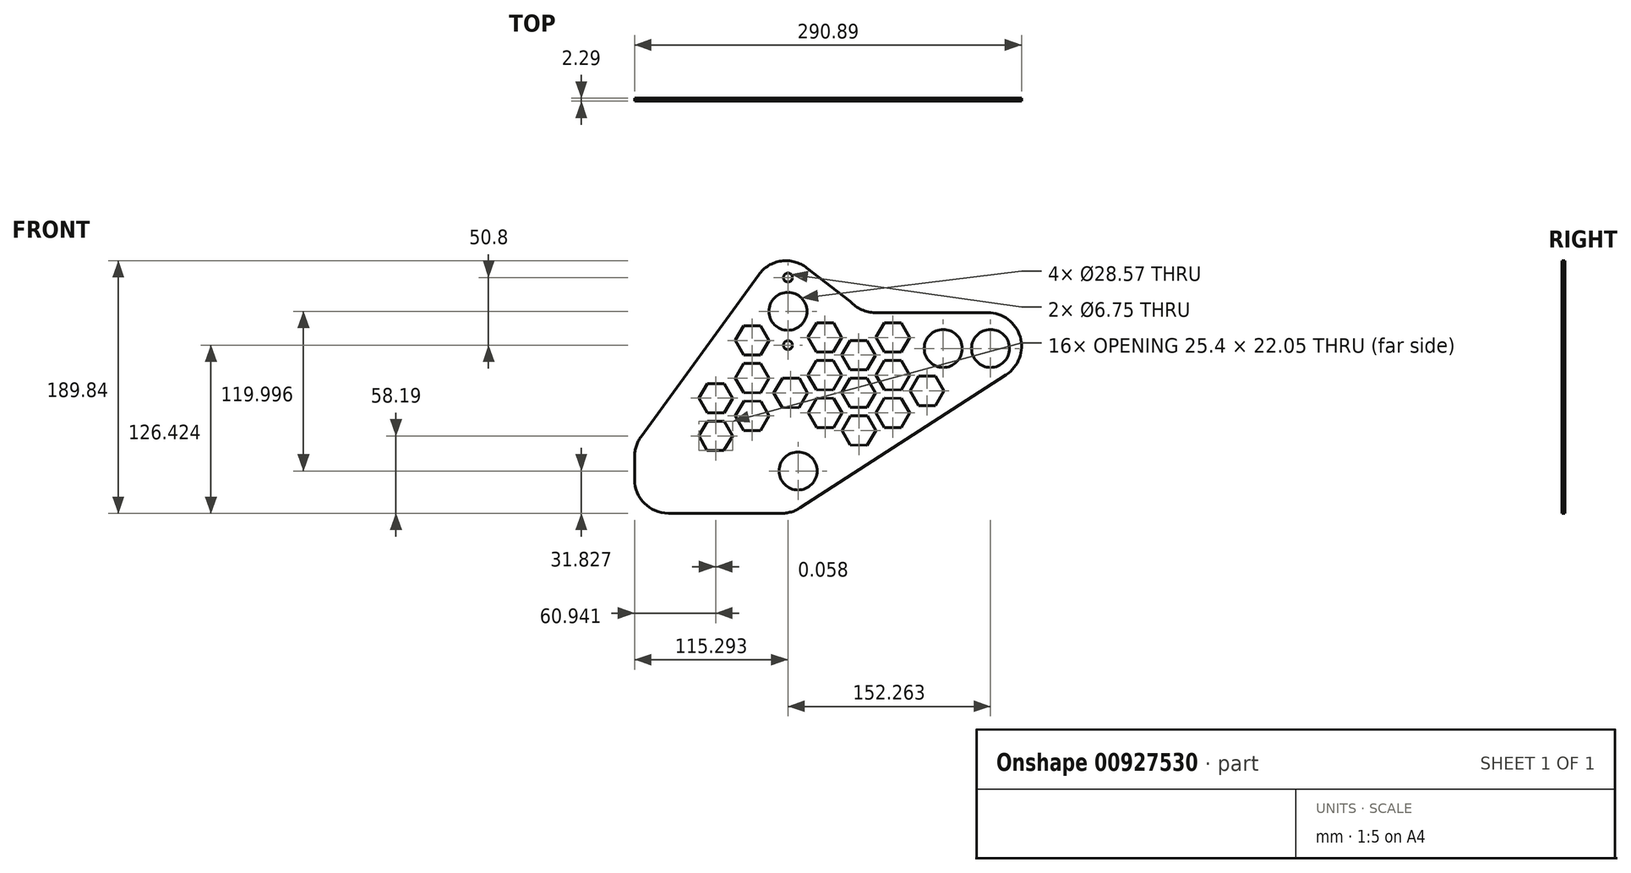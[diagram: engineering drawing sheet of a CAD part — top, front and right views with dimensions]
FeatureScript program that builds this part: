
annotation { "Feature Type Name" : "Feature", "Feature Type Description" : "" }
export const myFeature = defineFeature(function(context is Context, id is Id, definition is map)
    precondition{}
    {
        {
            var Q0;
            Q0=qCreatedBy(makeId("Front.planeOp"),FACE);
            var sketch = newSketch(context, id + "F0", { "sketchPlane" : qUnion([Q0])});
            skCircle(sketch, "E0", {"center": v(124.42, 56.16) * mm, "radius": 14.29 * mm});
            skCircle(sketch, "E1", {"center": v(88.86, 56.16) * mm, "radius": 14.29 * mm});
            skCircle(sketch, "E2", {"center": v(-27.85, 84.08) * mm, "radius": 14.29 * mm});
            skCircle(sketch, "E3", {"center": v(-20.21, -35.91) * mm, "radius": 14.29 * mm});
            skLineSegment(sketch, "E4", {"start": v(189.17, -93.06) * mm, "end": v(-151.78, -93.06) * mm});
            skCircle(sketch, "E5", {"center": v(-27.85, 109.48) * mm, "radius": 3.37 * mm});
            skCircle(sketch, "E6", {"center": v(-27.85, 58.68) * mm, "radius": 3.37 * mm});
            skLineSegment(sketch, "E7", {"start": v(-18.82, -63.68) * mm, "end": v(136.13, 36.41) * mm});
            skLineSegment(sketch, "E8", {"start": v(37.84, 83.15) * mm, "end": v(122.35, 83.15) * mm});
            skPoint(sketch, "E9.visualSharp", {"position": v(208.48, 83.15) * mm});
            skArc(sketch, "E9.filletArc", {"start": v(136.13, 36.41) * mm, "mid": v(146.71, 64.93) * mm, "end": v(122.35, 83.15) * mm});
            skPoint(sketch, "E10.visualSharp", {"position": v(26.59, 83.15) * mm});
            skArc(sketch, "E10.filletArc", {"start": v(19.03, 91.48) * mm, "mid": v(27.55, 85.33) * mm, "end": v(37.84, 83.15) * mm});
            skPoint(sketch, "E11.visualSharp", {"position": v(-170.89, -139.65) * mm});
            skPoint(sketch, "E12.visualSharp", {"position": v(-106.56, -106.37) * mm});
            skPoint(sketch, "E13.visualSharp", {"position": v(-22.67, -66.16) * mm});
            skArc(sketch, "E13.filletArc", {"start": v(-34.57, -67.66) * mm, "mid": v(-26.37, -66.96) * mm, "end": v(-18.82, -63.68) * mm});
            skCircle(sketch, "E14.cCircle", {"center": v(50.95, 64.44) * mm, "radius": 11 * mm, "construction": true});
            skLineSegment(sketch, "E14.0", {"start": v(44.55, 53.47) * mm, "end": v(38.25, 64.5) * mm});
            skLineSegment(sketch, "E14.1", {"start": v(38.25, 64.5) * mm, "end": v(44.64, 75.47) * mm});
            skLineSegment(sketch, "E14.2", {"start": v(44.64, 75.47) * mm, "end": v(57.34, 75.41) * mm});
            skLineSegment(sketch, "E14.3", {"start": v(57.34, 75.41) * mm, "end": v(63.65, 64.39) * mm});
            skLineSegment(sketch, "E14.4", {"start": v(63.65, 64.39) * mm, "end": v(57.25, 53.42) * mm});
            skLineSegment(sketch, "E14.5", {"start": v(57.25, 53.42) * mm, "end": v(44.55, 53.47) * mm});
            skPoint(sketch, "E14.0.midPoint", {"position": v(41.4, 58.99) * mm});
            skCircle(sketch, "E15.cCircle", {"center": v(50.89, 36.1) * mm, "radius": 11 * mm, "construction": true});
            skLineSegment(sketch, "E15.0", {"start": v(44.49, 25.13) * mm, "end": v(38.19, 36.15) * mm});
            skLineSegment(sketch, "E15.1", {"start": v(38.19, 36.15) * mm, "end": v(44.59, 47.12) * mm});
            skLineSegment(sketch, "E15.2", {"start": v(44.59, 47.12) * mm, "end": v(57.29, 47.07) * mm});
            skLineSegment(sketch, "E15.3", {"start": v(57.29, 47.07) * mm, "end": v(63.59, 36.04) * mm});
            skLineSegment(sketch, "E15.4", {"start": v(63.59, 36.04) * mm, "end": v(57.19, 25.07) * mm});
            skLineSegment(sketch, "E15.5", {"start": v(57.19, 25.07) * mm, "end": v(44.49, 25.13) * mm});
            skPoint(sketch, "E15.0.midPoint", {"position": v(41.34, 30.64) * mm});
            skCircle(sketch, "E16.cCircle", {"center": v(51.04, 7.75) * mm, "radius": 11 * mm, "construction": true});
            skLineSegment(sketch, "E16.0", {"start": v(44.64, -3.22) * mm, "end": v(38.34, 7.8) * mm});
            skLineSegment(sketch, "E16.1", {"start": v(38.34, 7.8) * mm, "end": v(44.74, 18.78) * mm});
            skLineSegment(sketch, "E16.2", {"start": v(44.74, 18.78) * mm, "end": v(57.44, 18.72) * mm});
            skLineSegment(sketch, "E16.3", {"start": v(57.44, 18.72) * mm, "end": v(63.74, 7.7) * mm});
            skLineSegment(sketch, "E16.4", {"start": v(63.74, 7.7) * mm, "end": v(57.34, -3.28) * mm});
            skLineSegment(sketch, "E16.5", {"start": v(57.34, -3.28) * mm, "end": v(44.64, -3.22) * mm});
            skPoint(sketch, "E16.0.midPoint", {"position": v(41.5, 2.3) * mm});
            skCircle(sketch, "E17.cCircle", {"center": v(25.33, 51.18) * mm, "radius": 11 * mm, "construction": true});
            skLineSegment(sketch, "E17.0", {"start": v(18.93, 40.2) * mm, "end": v(12.63, 51.23) * mm});
            skLineSegment(sketch, "E17.1", {"start": v(12.63, 51.23) * mm, "end": v(19.03, 62.2) * mm});
            skLineSegment(sketch, "E17.2", {"start": v(19.03, 62.2) * mm, "end": v(31.73, 62.15) * mm});
            skLineSegment(sketch, "E17.3", {"start": v(31.73, 62.15) * mm, "end": v(38.03, 51.12) * mm});
            skLineSegment(sketch, "E17.4", {"start": v(38.03, 51.12) * mm, "end": v(31.63, 40.15) * mm});
            skLineSegment(sketch, "E17.5", {"start": v(31.63, 40.15) * mm, "end": v(18.93, 40.2) * mm});
            skPoint(sketch, "E17.0.midPoint", {"position": v(15.78, 45.72) * mm});
            skCircle(sketch, "E18.cCircle", {"center": v(25.27, 22.83) * mm, "radius": 11 * mm, "construction": true});
            skLineSegment(sketch, "E18.0", {"start": v(18.87, 11.86) * mm, "end": v(12.57, 22.89) * mm});
            skLineSegment(sketch, "E18.1", {"start": v(12.57, 22.89) * mm, "end": v(18.97, 33.86) * mm});
            skLineSegment(sketch, "E18.2", {"start": v(18.97, 33.86) * mm, "end": v(31.67, 33.8) * mm});
            skLineSegment(sketch, "E18.3", {"start": v(31.67, 33.8) * mm, "end": v(37.97, 22.77) * mm});
            skLineSegment(sketch, "E18.4", {"start": v(37.97, 22.77) * mm, "end": v(31.57, 11.8) * mm});
            skLineSegment(sketch, "E18.5", {"start": v(31.57, 11.8) * mm, "end": v(18.87, 11.86) * mm});
            skPoint(sketch, "E18.0.midPoint", {"position": v(15.72, 17.37) * mm});
            skCircle(sketch, "E19.cCircle", {"center": v(25.42, -5.52) * mm, "radius": 11 * mm, "construction": true});
            skLineSegment(sketch, "E19.0", {"start": v(19.03, -16.49) * mm, "end": v(12.72, -5.46) * mm});
            skLineSegment(sketch, "E19.1", {"start": v(12.72, -5.46) * mm, "end": v(19.12, 5.51) * mm});
            skLineSegment(sketch, "E19.2", {"start": v(19.12, 5.51) * mm, "end": v(31.82, 5.45) * mm});
            skLineSegment(sketch, "E19.3", {"start": v(31.82, 5.45) * mm, "end": v(38.12, -5.57) * mm});
            skLineSegment(sketch, "E19.4", {"start": v(38.12, -5.57) * mm, "end": v(31.73, -16.54) * mm});
            skLineSegment(sketch, "E19.5", {"start": v(31.73, -16.54) * mm, "end": v(19.03, -16.49) * mm});
            skPoint(sketch, "E19.0.midPoint", {"position": v(15.88, -10.97) * mm});
            skCircle(sketch, "E20.cCircle", {"center": v(-0.02, 64.44) * mm, "radius": 11 * mm, "construction": true});
            skLineSegment(sketch, "E20.0", {"start": v(-6.42, 53.47) * mm, "end": v(-12.72, 64.5) * mm});
            skLineSegment(sketch, "E20.1", {"start": v(-12.72, 64.5) * mm, "end": v(-6.32, 75.47) * mm});
            skLineSegment(sketch, "E20.2", {"start": v(-6.32, 75.47) * mm, "end": v(6.38, 75.41) * mm});
            skLineSegment(sketch, "E20.3", {"start": v(6.38, 75.41) * mm, "end": v(12.68, 64.39) * mm});
            skLineSegment(sketch, "E20.4", {"start": v(12.68, 64.39) * mm, "end": v(6.28, 53.42) * mm});
            skLineSegment(sketch, "E20.5", {"start": v(6.28, 53.42) * mm, "end": v(-6.42, 53.47) * mm});
            skPoint(sketch, "E20.0.midPoint", {"position": v(-9.57, 58.99) * mm});
            skCircle(sketch, "E21.cCircle", {"center": v(-0.08, 36.1) * mm, "radius": 11 * mm, "construction": true});
            skLineSegment(sketch, "E21.0", {"start": v(-6.47, 25.13) * mm, "end": v(-12.77, 36.15) * mm});
            skLineSegment(sketch, "E21.1", {"start": v(-12.77, 36.15) * mm, "end": v(-6.38, 47.12) * mm});
            skLineSegment(sketch, "E21.2", {"start": v(-6.38, 47.12) * mm, "end": v(6.32, 47.07) * mm});
            skLineSegment(sketch, "E21.3", {"start": v(6.32, 47.07) * mm, "end": v(12.62, 36.04) * mm});
            skLineSegment(sketch, "E21.4", {"start": v(12.62, 36.04) * mm, "end": v(6.23, 25.07) * mm});
            skLineSegment(sketch, "E21.5", {"start": v(6.23, 25.07) * mm, "end": v(-6.47, 25.13) * mm});
            skPoint(sketch, "E21.0.midPoint", {"position": v(-9.62, 30.64) * mm});
            skCircle(sketch, "E22.cCircle", {"center": v(0.08, 7.75) * mm, "radius": 11 * mm, "construction": true});
            skLineSegment(sketch, "E22.0", {"start": v(-6.32, -3.22) * mm, "end": v(-12.62, 7.8) * mm});
            skLineSegment(sketch, "E22.1", {"start": v(-12.62, 7.8) * mm, "end": v(-6.22, 18.78) * mm});
            skLineSegment(sketch, "E22.2", {"start": v(-6.22, 18.78) * mm, "end": v(6.48, 18.72) * mm});
            skLineSegment(sketch, "E22.3", {"start": v(6.48, 18.72) * mm, "end": v(12.78, 7.7) * mm});
            skLineSegment(sketch, "E22.4", {"start": v(12.78, 7.7) * mm, "end": v(6.38, -3.28) * mm});
            skLineSegment(sketch, "E22.5", {"start": v(6.38, -3.28) * mm, "end": v(-6.32, -3.22) * mm});
            skPoint(sketch, "E22.0.midPoint", {"position": v(-9.47, 2.3) * mm});
            skCircle(sketch, "E23.cCircle", {"center": v(-25.75, 22.77) * mm, "radius": 11 * mm, "construction": true});
            skLineSegment(sketch, "E23.0", {"start": v(-32.14, 11.8) * mm, "end": v(-38.44, 22.83) * mm});
            skLineSegment(sketch, "E23.1", {"start": v(-38.44, 22.83) * mm, "end": v(-32.05, 33.8) * mm});
            skLineSegment(sketch, "E23.2", {"start": v(-32.05, 33.8) * mm, "end": v(-19.35, 33.74) * mm});
            skLineSegment(sketch, "E23.3", {"start": v(-19.35, 33.74) * mm, "end": v(-13.05, 22.72) * mm});
            skLineSegment(sketch, "E23.4", {"start": v(-13.05, 22.72) * mm, "end": v(-19.44, 11.75) * mm});
            skLineSegment(sketch, "E23.5", {"start": v(-19.44, 11.75) * mm, "end": v(-32.14, 11.8) * mm});
            skPoint(sketch, "E23.0.midPoint", {"position": v(-35.3, 17.32) * mm});
            skCircle(sketch, "E24.cCircle", {"center": v(-54.74, 62.2) * mm, "radius": 11 * mm, "construction": true});
            skLineSegment(sketch, "E24.0", {"start": v(-61.14, 51.23) * mm, "end": v(-67.44, 62.26) * mm});
            skLineSegment(sketch, "E24.1", {"start": v(-67.44, 62.26) * mm, "end": v(-61.04, 73.23) * mm});
            skLineSegment(sketch, "E24.2", {"start": v(-61.04, 73.23) * mm, "end": v(-48.34, 73.17) * mm});
            skLineSegment(sketch, "E24.3", {"start": v(-48.34, 73.17) * mm, "end": v(-42.04, 62.15) * mm});
            skLineSegment(sketch, "E24.4", {"start": v(-42.04, 62.15) * mm, "end": v(-48.44, 51.18) * mm});
            skLineSegment(sketch, "E24.5", {"start": v(-48.44, 51.18) * mm, "end": v(-61.14, 51.23) * mm});
            skPoint(sketch, "E24.0.midPoint", {"position": v(-64.3, 56.75) * mm});
            skCircle(sketch, "E25.cCircle", {"center": v(-54.8, 33.86) * mm, "radius": 11 * mm, "construction": true});
            skLineSegment(sketch, "E25.0", {"start": v(-61.2, 22.89) * mm, "end": v(-67.5, 33.91) * mm});
            skLineSegment(sketch, "E25.1", {"start": v(-67.5, 33.91) * mm, "end": v(-61.1, 44.88) * mm});
            skLineSegment(sketch, "E25.2", {"start": v(-61.1, 44.88) * mm, "end": v(-48.4, 44.83) * mm});
            skLineSegment(sketch, "E25.3", {"start": v(-48.4, 44.83) * mm, "end": v(-42.1, 33.8) * mm});
            skLineSegment(sketch, "E25.4", {"start": v(-42.1, 33.8) * mm, "end": v(-48.5, 22.83) * mm});
            skLineSegment(sketch, "E25.5", {"start": v(-48.5, 22.83) * mm, "end": v(-61.2, 22.89) * mm});
            skPoint(sketch, "E25.0.midPoint", {"position": v(-64.35, 28.4) * mm});
            skCircle(sketch, "E26.cCircle", {"center": v(-54.65, 5.51) * mm, "radius": 11 * mm, "construction": true});
            skLineSegment(sketch, "E26.0", {"start": v(-61.04, -5.46) * mm, "end": v(-67.35, 5.57) * mm});
            skLineSegment(sketch, "E26.1", {"start": v(-67.35, 5.57) * mm, "end": v(-60.95, 16.54) * mm});
            skLineSegment(sketch, "E26.2", {"start": v(-60.95, 16.54) * mm, "end": v(-48.25, 16.48) * mm});
            skLineSegment(sketch, "E26.3", {"start": v(-48.25, 16.48) * mm, "end": v(-41.95, 5.45) * mm});
            skLineSegment(sketch, "E26.4", {"start": v(-41.95, 5.45) * mm, "end": v(-48.34, -5.52) * mm});
            skLineSegment(sketch, "E26.5", {"start": v(-48.34, -5.52) * mm, "end": v(-61.04, -5.46) * mm});
            skPoint(sketch, "E26.0.midPoint", {"position": v(-64.2, 0.05) * mm});
            skCircle(sketch, "E27.cCircle", {"center": v(-82.14, 18.8) * mm, "radius": 11 * mm, "construction": true});
            skLineSegment(sketch, "E27.0", {"start": v(-88.54, 7.83) * mm, "end": v(-94.84, 18.85) * mm});
            skLineSegment(sketch, "E27.1", {"start": v(-94.84, 18.85) * mm, "end": v(-88.44, 29.82) * mm});
            skLineSegment(sketch, "E27.2", {"start": v(-88.44, 29.82) * mm, "end": v(-75.74, 29.77) * mm});
            skLineSegment(sketch, "E27.3", {"start": v(-75.74, 29.77) * mm, "end": v(-69.44, 18.74) * mm});
            skLineSegment(sketch, "E27.4", {"start": v(-69.44, 18.74) * mm, "end": v(-75.84, 7.77) * mm});
            skLineSegment(sketch, "E27.5", {"start": v(-75.84, 7.77) * mm, "end": v(-88.54, 7.83) * mm});
            skPoint(sketch, "E27.0.midPoint", {"position": v(-91.7, 13.34) * mm});
            skCircle(sketch, "E28.cCircle", {"center": v(-82.2, -9.55) * mm, "radius": 11 * mm, "construction": true});
            skLineSegment(sketch, "E28.0", {"start": v(-88.6, -20.52) * mm, "end": v(-94.9, -9.5) * mm});
            skLineSegment(sketch, "E28.1", {"start": v(-94.9, -9.5) * mm, "end": v(-88.5, 1.48) * mm});
            skLineSegment(sketch, "E28.2", {"start": v(-88.5, 1.48) * mm, "end": v(-75.8, 1.42) * mm});
            skLineSegment(sketch, "E28.3", {"start": v(-75.8, 1.42) * mm, "end": v(-69.5, -9.6) * mm});
            skLineSegment(sketch, "E28.4", {"start": v(-69.5, -9.6) * mm, "end": v(-75.9, -20.58) * mm});
            skLineSegment(sketch, "E28.5", {"start": v(-75.9, -20.58) * mm, "end": v(-88.6, -20.52) * mm});
            skPoint(sketch, "E28.0.midPoint", {"position": v(-91.75, -15) * mm});
            skPoint(sketch, "E29.0.midPoint", {"position": v(-9.37, -25.84) * mm});
            skCircle(sketch, "E30.cCircle", {"center": v(76.75, 24.31) * mm, "radius": 11 * mm, "construction": true});
            skLineSegment(sketch, "E30.0", {"start": v(70.35, 13.34) * mm, "end": v(64.05, 24.37) * mm});
            skLineSegment(sketch, "E30.1", {"start": v(64.05, 24.37) * mm, "end": v(70.44, 35.34) * mm});
            skLineSegment(sketch, "E30.2", {"start": v(70.44, 35.34) * mm, "end": v(83.14, 35.28) * mm});
            skLineSegment(sketch, "E30.3", {"start": v(83.14, 35.28) * mm, "end": v(89.45, 24.25) * mm});
            skLineSegment(sketch, "E30.4", {"start": v(89.45, 24.25) * mm, "end": v(83.05, 13.28) * mm});
            skLineSegment(sketch, "E30.5", {"start": v(83.05, 13.28) * mm, "end": v(70.35, 13.34) * mm});
            skPoint(sketch, "E30.0.midPoint", {"position": v(67.2, 18.85) * mm});
            skLineSegment(sketch, "E31", {"start": v(-34.57, -67.66) * mm, "end": v(-117.74, -67.66) * mm});
            skLineSegment(sketch, "E32", {"start": v(-143.14, -42.26) * mm, "end": v(-143.14, -25.11) * mm});
            skLineSegment(sketch, "E33", {"start": v(-138.3, -10.19) * mm, "end": v(-49.82, 111.62) * mm});
            skLineSegment(sketch, "E34", {"start": v(19.03, 91.48) * mm, "end": v(-13.74, 116.8) * mm});
            skPoint(sketch, "E35.visualSharp", {"position": v(-34.45, 132.8) * mm});
            skArc(sketch, "E35.filletArc", {"start": v(-13.74, 116.8) * mm, "mid": v(-32.88, 121.84) * mm, "end": v(-49.82, 111.62) * mm});
            skPoint(sketch, "E36.visualSharp", {"position": v(-143.14, -67.66) * mm});
            skArc(sketch, "E36.filletArc", {"start": v(-143.14, -42.26) * mm, "mid": v(-135.7, -60.22) * mm, "end": v(-117.74, -67.66) * mm});
            skPoint(sketch, "E37.visualSharp", {"position": v(-143.14, -16.86) * mm});
            skArc(sketch, "E37.filletArc", {"start": v(-138.3, -10.19) * mm, "mid": v(-141.9, -17.27) * mm, "end": v(-143.14, -25.11) * mm});
            skSolve(sketch);
        }
        {
            var Q0;
            Q0=makeQuery(id+"F0.imprint","IMPRINT",FACE,{"disambiguationData":[TD([[makeQuery(id+"F0.imprint","IMPRINT",EDGE,{"derivedFrom":sQuery(id+"F0.wireOp",EDGE,"E0")}),-1.0]])]});
            extrude(context, id + "F1", {"entities" : qUnion([Q0]), "depth" : 2.3 * mm, "offsetDistance" : 25.4 * mm});
        }
    });
